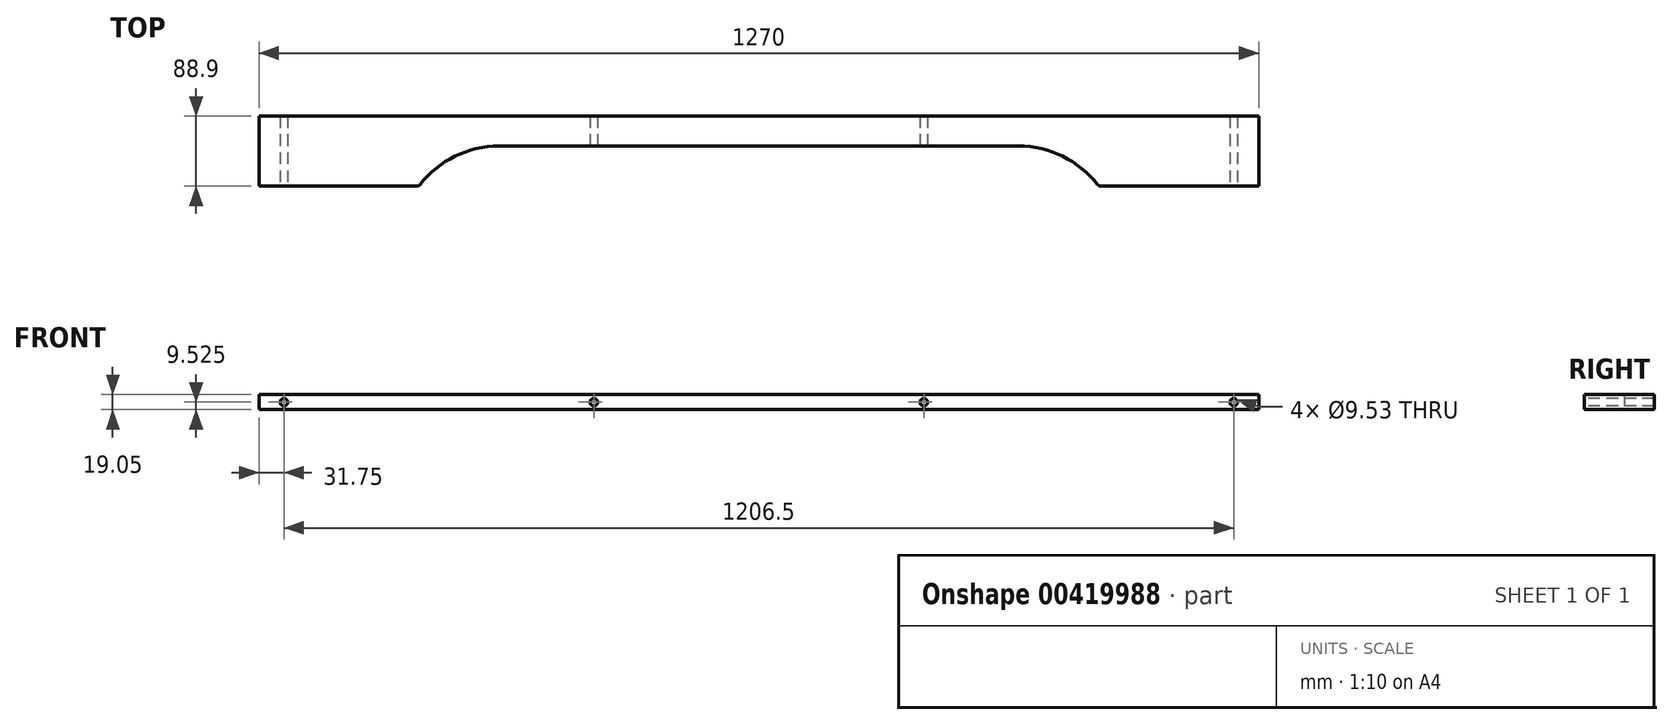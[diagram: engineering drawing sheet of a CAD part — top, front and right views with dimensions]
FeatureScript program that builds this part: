
annotation { "Feature Type Name" : "Feature", "Feature Type Description" : "" }
export const myFeature = defineFeature(function(context is Context, id is Id, definition is map)
    precondition{}
    {
        {
            var Q0;
            Q0=qCreatedBy(makeId("Top.planeOp"),FACE);
            var sketch = newSketch(context, id + "F0", { "sketchPlane" : qUnion([Q0])});
            skLineSegment(sketch, "E0.bottom", {"start": v(0, 0) * mm, "end": v(203.2, 0) * mm});
            skLineSegment(sketch, "E0.top", {"start": v(0, 88.9) * mm, "end": v(1270, 88.9) * mm});
            skLineSegment(sketch, "E0.left", {"start": v(0, 0) * mm, "end": v(0, 88.9) * mm});
            skLineSegment(sketch, "E0.right", {"start": v(1270, 0) * mm, "end": v(1270, 88.9) * mm});
            skLineSegment(sketch, "E1", {"start": v(304.8, 50.8) * mm, "end": v(965.2, 50.8) * mm});
            skArc(sketch, "E2", {"start": v(304.8, 50.8) * mm, "mid": v(248, 37.4) * mm, "end": v(203.2, 0) * mm});
            skArc(sketch, "E3", {"start": v(965.2, 50.8) * mm, "mid": v(1022, 37.4) * mm, "end": v(1066.8, 0) * mm});
            skLineSegment(sketch, "E4", {"start": v(1066.8, 0) * mm, "end": v(1270, 0) * mm});
            skSolve(sketch);
        }
        {
            var Q0;
            Q0=makeQuery(id+"F0.imprint","IMPRINT",FACE,{"disambiguationData":[TD([[makeQuery(id+"F0.imprint","IMPRINT",EDGE,{"derivedFrom":sQuery(id+"F0.wireOp",EDGE,"E0.bottom")}),1.0]])]});
            extrude(context, id + "F1", {"entities" : qUnion([Q0]), "depth" : 19.05 * mm});
        }
        {
            var Q0;
            Q0=makeQuery(id+"F1.opExtrude","SWEPT_FACE",FACE,{"disambiguationData":[OSD([sQuery(id+"F0.wireOp",EDGE,"E0.bottom")])]});
            var sketch = newSketch(context, id + "F2", { "sketchPlane" : qUnion([Q0])});
            skCircle(sketch, "E5", {"center": v(31.75, 9.52) * mm, "radius": 4.76 * mm});
            skCircle(sketch, "E6", {"center": v(425.45, 9.53) * mm, "radius": 4.76 * mm});
            skLineSegment(sketch, "E7", {"start": v(0, 9.52) * mm, "end": v(1270, 9.53) * mm, "construction": true});
            skCircle(sketch, "E8.MirrorC", {"center": v(844.55, 9.53) * mm, "radius": 4.76 * mm});
            skCircle(sketch, "E9.MirrorC", {"center": v(1238.25, 9.53) * mm, "radius": 4.76 * mm});
            skSolve(sketch);
        }
        {
            var Q0;
            Q0=sQuery(id+"F2.wireOp",VERTEX,"E5.center");
            var Q1;
            Q1=sQuery(id+"F2.wireOp",VERTEX,"E6.center");
            var Q2;
            Q2=sQuery(id+"F2.wireOp",VERTEX,"E8.MirrorC.center");
            var Q3;
            Q3=sQuery(id+"F2.wireOp",VERTEX,"E9.MirrorC.center");
            var Q4;
            Q4=makeQuery(id+"F1.opExtrude","SWEPT_BODY",BODY,{"disambiguationData":[OSD([sQuery(id+"F0.wireOp",EDGE,"E0.bottom"),sQuery(id+"F0.wireOp",EDGE,"E0.top"),sQuery(id+"F0.wireOp",EDGE,"E0.left"),sQuery(id+"F0.wireOp",EDGE,"E0.right")])]});
            hole(context, id + "F3", {"style" : HoleStyle.SIMPLE, "endStyle" : HoleEndStyle.THROUGH, "holeDiameter" : 9.52 * mm, "isTappedThrough" : true, "tappedDepth" : 12.7 * mm, "tapClearance" : 3, "locations" : qUnion([Q0, Q1, Q2, Q3]), "scope" : qUnion([Q4])});
        }
        {
            var Q0;
            Q0=makeQuery(id+"F1.opExtrude","SWEPT_EDGE",EDGE,{"disambiguationData":[OSD([sQuery(id+"F0.wireOp",EDGE,"E0.bottom"),sQuery(id+"F0.wireOp",EDGE,"E2")])]});
            var Q1;
            Q1=makeQuery(id+"F1.opExtrude","SWEPT_EDGE",EDGE,{"disambiguationData":[OSD([sQuery(id+"F0.wireOp",EDGE,"E3"),sQuery(id+"F0.wireOp",EDGE,"E4")])]});
            fillet(context, id + "F4", {"entities" : qUnion([Q0, Q1]), "radius" : 5.08 * mm, "tangentPropagation" : true, "allowEdgeOverflow" : false});
        }
    });
